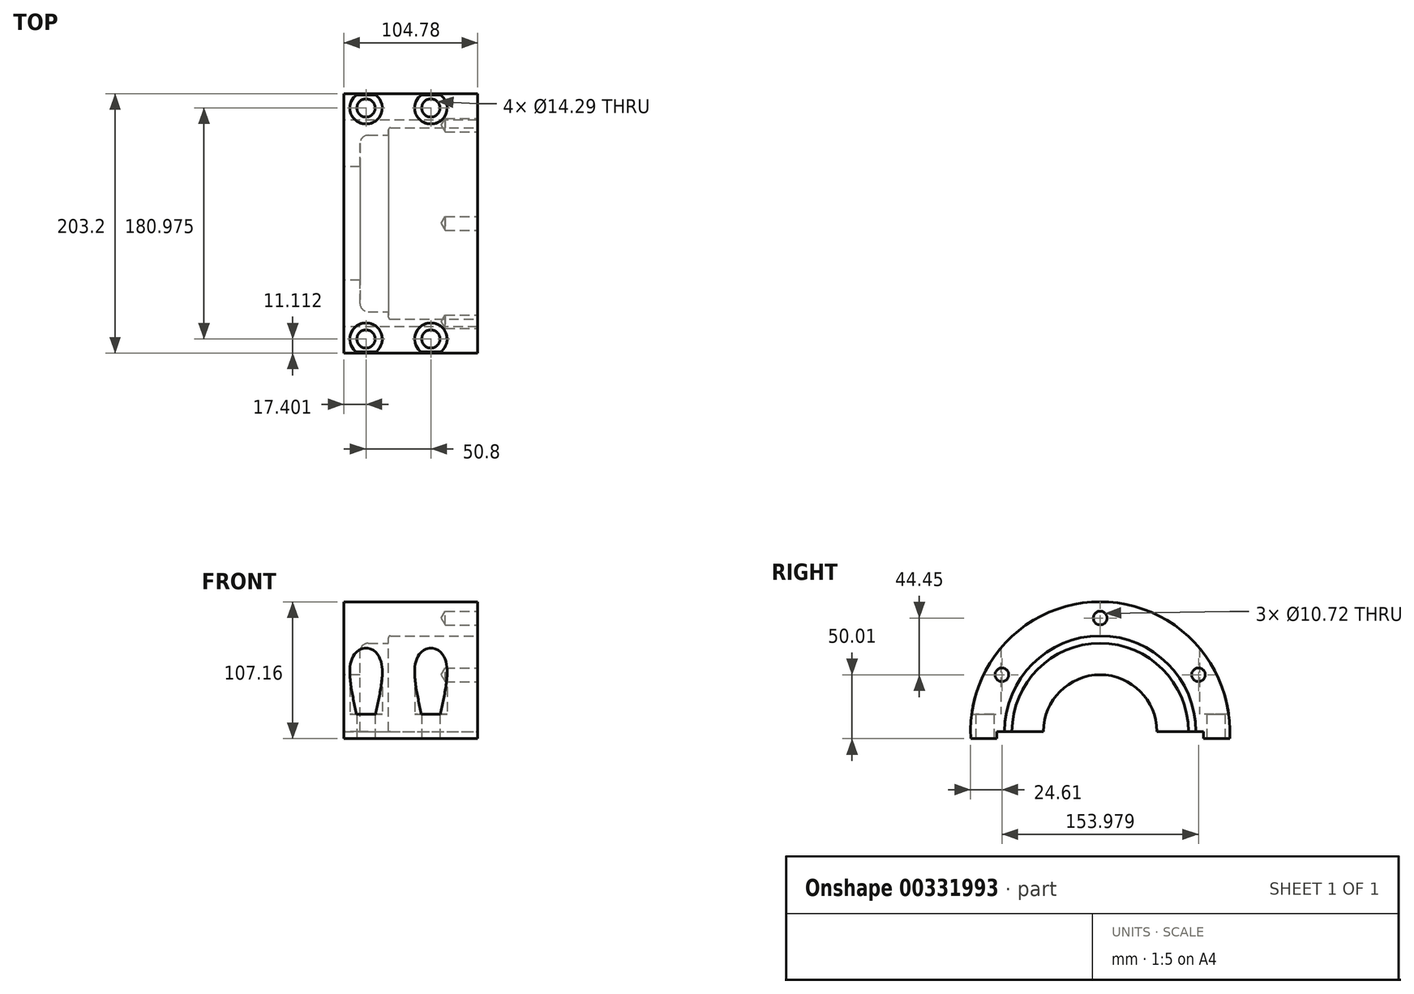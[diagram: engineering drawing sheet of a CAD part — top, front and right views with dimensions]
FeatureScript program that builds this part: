
annotation { "Feature Type Name" : "Feature", "Feature Type Description" : "" }
export const myFeature = defineFeature(function(context is Context, id is Id, definition is map)
    precondition{}
    {
        {
            var Q0;
            Q0=qCreatedBy(makeId("Right.planeOp"),FACE);
            var sketch = newSketch(context, id + "F0", { "sketchPlane" : qUnion([Q0])});
            skCircle(sketch, "E0", {"center": v(0, 0) * mm, "radius": 101.6 * mm});
            skCircle(sketch, "E1", {"center": v(0, 0) * mm, "radius": 44.45 * mm});
            skSolve(sketch);
        }
        {
            var Q0;
            Q0 = qSketchRegion(id + "F0", true);
            extrude(context, id + "F1", {"entities" : qUnion([Q0]), "endBound" : BoundingType.SYMMETRIC, "depth" : 104.77 * mm});
        }
        {
            var Q0;
            Q0=makeQuery(id+"F1.opExtrude","CAP_FACE",FACE,{"disambiguationData":[OSD([sQuery(id+"F0.wireOp",EDGE,"E0"),sQuery(id+"F0.wireOp",EDGE,"E1")])],"isStart":false});
            var sketch = newSketch(context, id + "F2", { "sketchPlane" : qUnion([Q0])});
            skCircle(sketch, "E2", {"center": v(0, 0) * mm, "radius": 69.09 * mm});
            skSolve(sketch);
        }
        {
            var Q0;
            Q0 = qSketchRegion(id + "F2", true);
            extrude(context, id + "F3", {"entities" : qUnion([Q0]), "operationType" : NewBodyOperationType.REMOVE, "oppositeDirection" : true, "depth" : 92.07 * mm});
        }
        {
            var Q0;
            Q0=makeQuery(id+"F1.opExtrude","CAP_FACE",FACE,{"disambiguationData":[OSD([sQuery(id+"F0.wireOp",EDGE,"E0"),sQuery(id+"F0.wireOp",EDGE,"E1")])],"isStart":false});
            var sketch = newSketch(context, id + "F4", { "sketchPlane" : qUnion([Q0])});
            skCircle(sketch, "E3", {"center": v(0, 0) * mm, "radius": 74.93 * mm});
            skSolve(sketch);
        }
        {
            var Q0;
            Q0 = qSketchRegion(id + "F4", true);
            extrude(context, id + "F5", {"entities" : qUnion([Q0]), "operationType" : NewBodyOperationType.REMOVE, "oppositeDirection" : true, "depth" : 69.85 * mm});
        }
        {
            var Q0;
            Q0=makeQuery(id+"F3.boolean.opBoolean","COPY",EDGE,{"derivedFrom":makeQuery(id+"F3.opExtrude","CAP_EDGE",EDGE,{"disambiguationData":[OSD([sQuery(id+"F2.wireOp",EDGE,"E2")])],"isStart":false})});
            fillet(context, id + "F6", {"entities" : qUnion([Q0]), "radius" : 6.35 * mm, "tangentPropagation" : true, "allowEdgeOverflow" : false});
        }
        {
            var Q0;
            Q0=makeQuery(id+"F5.boolean.opBoolean","COPY",EDGE,{"derivedFrom":makeQuery(id+"F5.opExtrude","CAP_EDGE",EDGE,{"disambiguationData":[OSD([sQuery(id+"F4.wireOp",EDGE,"E3")])],"isStart":false})});
            fillet(context, id + "F7", {"entities" : qUnion([Q0]), "radius" : 1.59 * mm, "tangentPropagation" : true, "allowEdgeOverflow" : false});
        }
        {
            var Q0;
            Q0=makeQuery(id+"F1.opExtrude","CAP_FACE",FACE,{"disambiguationData":[OSD([sQuery(id+"F0.wireOp",EDGE,"E0"),sQuery(id+"F0.wireOp",EDGE,"E1")])],"isStart":false});
            var sketch = newSketch(context, id + "F8", { "sketchPlane" : qUnion([Q0])});
            skCircle(sketch, "E4", {"center": v(0, 0) * mm, "radius": 88.9 * mm, "construction": true});
            skLineSegment(sketch, "E5", {"start": v(0, 0) * mm, "end": v(0, 117.43) * mm, "construction": true});
            skLineSegment(sketch, "E6", {"start": v(0, 0) * mm, "end": v(-111.63, 64.45) * mm, "construction": true});
            skPoint(sketch, "E7", {"position": v(-76.99, 44.45) * mm});
            skPoint(sketch, "E8", {"position": v(0, 88.9) * mm});
            skPoint(sketch, "E9.MirrorP", {"position": v(76.99, 44.45) * mm});
            skSolve(sketch);
        }
        {
            var Q0;
            Q0=sQuery(id+"F8.wireOp",VERTEX,"E7");
            var Q1;
            Q1=sQuery(id+"F8.wireOp",VERTEX,"E8");
            var Q2;
            Q2=sQuery(id+"F8.wireOp",VERTEX,"E9.MirrorP");
            var Q3;
            Q3=makeQuery(id+"F1.opExtrude","SWEPT_BODY",BODY,{"disambiguationData":[OSD([sQuery(id+"F0.wireOp",EDGE,"E0"),sQuery(id+"F0.wireOp",EDGE,"E1")])]});
            hole(context, id + "F9", {"style" : HoleStyle.SIMPLE, "endStyle" : HoleEndStyle.BLIND, "standardTappedOrClearance" : lookupTablePath({ "standard" : "ANSI", "engagement" : "75%", "pitch" : "13 tpi", "size" : "1/2", "type" : "Tapped" }), "standardBlindInLast" : lookupTablePath({ "standard" : "ANSI", "engagement" : "75%", "pitch" : "13 tpi", "size" : "1/2", "type" : "Tapped" }), "holeDiameter" : 10.72 * mm, "showTappedDepth" : true, "holeDepth" : 25.4 * mm, "tappedDepth" : 19.53 * mm, "tapClearance" : 3, "locations" : qUnion([Q0, Q1, Q2]), "scope" : qUnion([Q3]), "majorDiameter" : 12.7 * mm});
        }
        {
            var Q0;
            Q0=makeQuery(id+"F1.opExtrude","CAP_FACE",FACE,{"disambiguationData":[OSD([sQuery(id+"F0.wireOp",EDGE,"E0"),sQuery(id+"F0.wireOp",EDGE,"E1")])],"isStart":false});
            var sketch = newSketch(context, id + "F10", { "sketchPlane" : qUnion([Q0])});
            skLineSegment(sketch, "E10", {"start": v(-153.72, 0) * mm, "end": v(137.98, 0) * mm, "construction": true});
            skLineSegment(sketch, "E11.0", {"start": v(-153.72, -5.56) * mm, "end": v(137.98, -5.56) * mm, "construction": true});
            skLineSegment(sketch, "E12.bottom", {"start": v(-150.99, -5.56) * mm, "end": v(143.45, -5.56) * mm});
            skLineSegment(sketch, "E12.top", {"start": v(-150.99, -114.35) * mm, "end": v(143.45, -114.35) * mm});
            skLineSegment(sketch, "E12.left", {"start": v(-150.99, -5.56) * mm, "end": v(-150.99, -114.35) * mm});
            skLineSegment(sketch, "E12.right", {"start": v(143.45, -5.56) * mm, "end": v(143.45, -114.35) * mm});
            skSolve(sketch);
        }
        {
            var Q0;
            Q0 = qSketchRegion(id + "F10", true);
            extrude(context, id + "F11", {"entities" : qUnion([Q0]), "operationType" : NewBodyOperationType.REMOVE, "endBound" : BoundingType.THROUGH_ALL, "oppositeDirection" : true, "depth" : 25.4 * mm});
        }
        {
            var Q0;
            Q0=makeQuery(id+"F1.opExtrude","CAP_FACE",FACE,{"disambiguationData":[OSD([sQuery(id+"F0.wireOp",EDGE,"E0"),sQuery(id+"F0.wireOp",EDGE,"E1")])],"isStart":false});
            var sketch = newSketch(context, id + "F12", { "sketchPlane" : qUnion([Q0])});
            skLineSegment(sketch, "E13", {"start": v(-147.56, 0) * mm, "end": v(159.2, 0) * mm, "construction": true});
            skLineSegment(sketch, "E14", {"start": v(0, 129.5) * mm, "end": v(0, -54.35) * mm, "construction": true});
            skLineSegment(sketch, "E15.0", {"start": v(-80.96, 129.5) * mm, "end": v(-80.96, -54.35) * mm, "construction": true});
            skLineSegment(sketch, "E16.bottom", {"start": v(-80.96, 0) * mm, "end": v(80.96, 0) * mm});
            skLineSegment(sketch, "E16.top", {"start": v(-80.96, -25.4) * mm, "end": v(80.96, -25.4) * mm});
            skLineSegment(sketch, "E16.left", {"start": v(-80.96, 0) * mm, "end": v(-80.96, -25.4) * mm});
            skLineSegment(sketch, "E16.right", {"start": v(80.96, 0) * mm, "end": v(80.96, -25.4) * mm});
            skSolve(sketch);
        }
        {
            var Q0;
            Q0 = qSketchRegion(id + "F12", true);
            extrude(context, id + "F13", {"entities" : qUnion([Q0]), "operationType" : NewBodyOperationType.REMOVE, "endBound" : BoundingType.THROUGH_ALL, "oppositeDirection" : true, "depth" : 25.4 * mm});
        }
        {
            var Q0;
            Q0=makeQuery(id+"F11.boolean.opBoolean","COPY",FACE,{"disambiguationData":[OD(0.0)],"derivedFrom":makeQuery(id+"F11.opExtrude","SWEPT_FACE",FACE,{"disambiguationData":[OSD([sQuery(id+"F10.wireOp",EDGE,"E12.bottom")])]})});
            var sketch = newSketch(context, id + "F14", { "sketchPlane" : qUnion([Q0])});
            skLineSegment(sketch, "E17.0", {"start": v(15.81, 101.45) * mm, "end": v(15.81, 80.96) * mm, "construction": true});
            skLineSegment(sketch, "E18.0", {"start": v(-34.99, 101.45) * mm, "end": v(-34.99, 80.96) * mm, "construction": true});
            skLineSegment(sketch, "E19", {"start": v(92.44, 0) * mm, "end": v(-99.97, 0) * mm, "construction": true});
            skLineSegment(sketch, "E20.0", {"start": v(92.44, 90.49) * mm, "end": v(-99.97, 90.49) * mm, "construction": true});
            skPoint(sketch, "E21", {"position": v(15.81, 90.49) * mm});
            skPoint(sketch, "E22", {"position": v(-34.99, 90.49) * mm});
            skPoint(sketch, "E23.MirrorP", {"position": v(15.81, -90.49) * mm});
            skPoint(sketch, "E24.MirrorP", {"position": v(-34.99, -90.49) * mm});
            skSolve(sketch);
        }
        {
            var Q0;
            Q0=sQuery(id+"F14.wireOp",VERTEX,"E21");
            var Q1;
            Q1=sQuery(id+"F14.wireOp",VERTEX,"E22");
            var Q2;
            Q2=sQuery(id+"F14.wireOp",VERTEX,"E23.MirrorP");
            var Q3;
            Q3=sQuery(id+"F14.wireOp",VERTEX,"E24.MirrorP");
            var Q4;
            Q4=makeQuery(id+"F1.opExtrude","SWEPT_BODY",BODY,{"disambiguationData":[OSD([sQuery(id+"F0.wireOp",EDGE,"E0"),sQuery(id+"F0.wireOp",EDGE,"E1")])]});
            hole(context, id + "F15", {"style" : HoleStyle.SIMPLE, "endStyle" : HoleEndStyle.THROUGH, "holeDiameter" : 14.29 * mm, "tappedDepth" : 19.54 * mm, "tapClearance" : 3, "locations" : qUnion([Q0, Q1, Q2, Q3]), "scope" : qUnion([Q4])});
        }
        {
            var Q0;
            Q0=makeQuery(id+"F11.boolean.opBoolean","COPY",FACE,{"disambiguationData":[OD(0.0)],"derivedFrom":makeQuery(id+"F11.opExtrude","SWEPT_FACE",FACE,{"disambiguationData":[OSD([sQuery(id+"F10.wireOp",EDGE,"E12.bottom")])]})});
            cPlane(context, id + "F16", {"entities" : qUnion([Q0]), "cplaneType" : CPlaneType.OFFSET, "offset" : 19.05 * mm, "oppositeDirection" : true, "width" : 152.4 * mm, "height" : 152.4 * mm});
        }
        {
            var Q0;
            Q0=qCreatedBy(id+"F16.planeOp",FACE);
            var sketch = newSketch(context, id + "F17", { "sketchPlane" : qUnion([Q0])});
            skLineSegment(sketch, "E25", {"start": v(-131.89, 0) * mm, "end": v(145.82, 0) * mm, "construction": true});
            skCircle(sketch, "E26.0", {"center": v(-34.99, 90.49) * mm, "radius": 7.14 * mm, "construction": true});
            skCircle(sketch, "E27.0", {"center": v(15.81, 90.49) * mm, "radius": 7.14 * mm, "construction": true});
            skCircle(sketch, "E28.0", {"center": v(15.81, -90.49) * mm, "radius": 7.14 * mm, "construction": true});
            skCircle(sketch, "E29.0", {"center": v(-34.99, -90.49) * mm, "radius": 7.14 * mm, "construction": true});
            skCircle(sketch, "E30", {"center": v(-34.99, 90.49) * mm, "radius": 12.7 * mm});
            skCircle(sketch, "E31", {"center": v(15.81, 90.49) * mm, "radius": 12.7 * mm});
            skCircle(sketch, "E32", {"center": v(-34.99, -90.49) * mm, "radius": 12.7 * mm});
            skCircle(sketch, "E33", {"center": v(15.81, -90.49) * mm, "radius": 12.7 * mm});
            skSolve(sketch);
        }
        {
            var Q0;
            Q0 = qSketchRegion(id + "F17", true);
            extrude(context, id + "F18", {"entities" : qUnion([Q0]), "operationType" : NewBodyOperationType.REMOVE, "endBound" : BoundingType.THROUGH_ALL, "oppositeDirection" : true, "depth" : 25.4 * mm});
        }
    });
